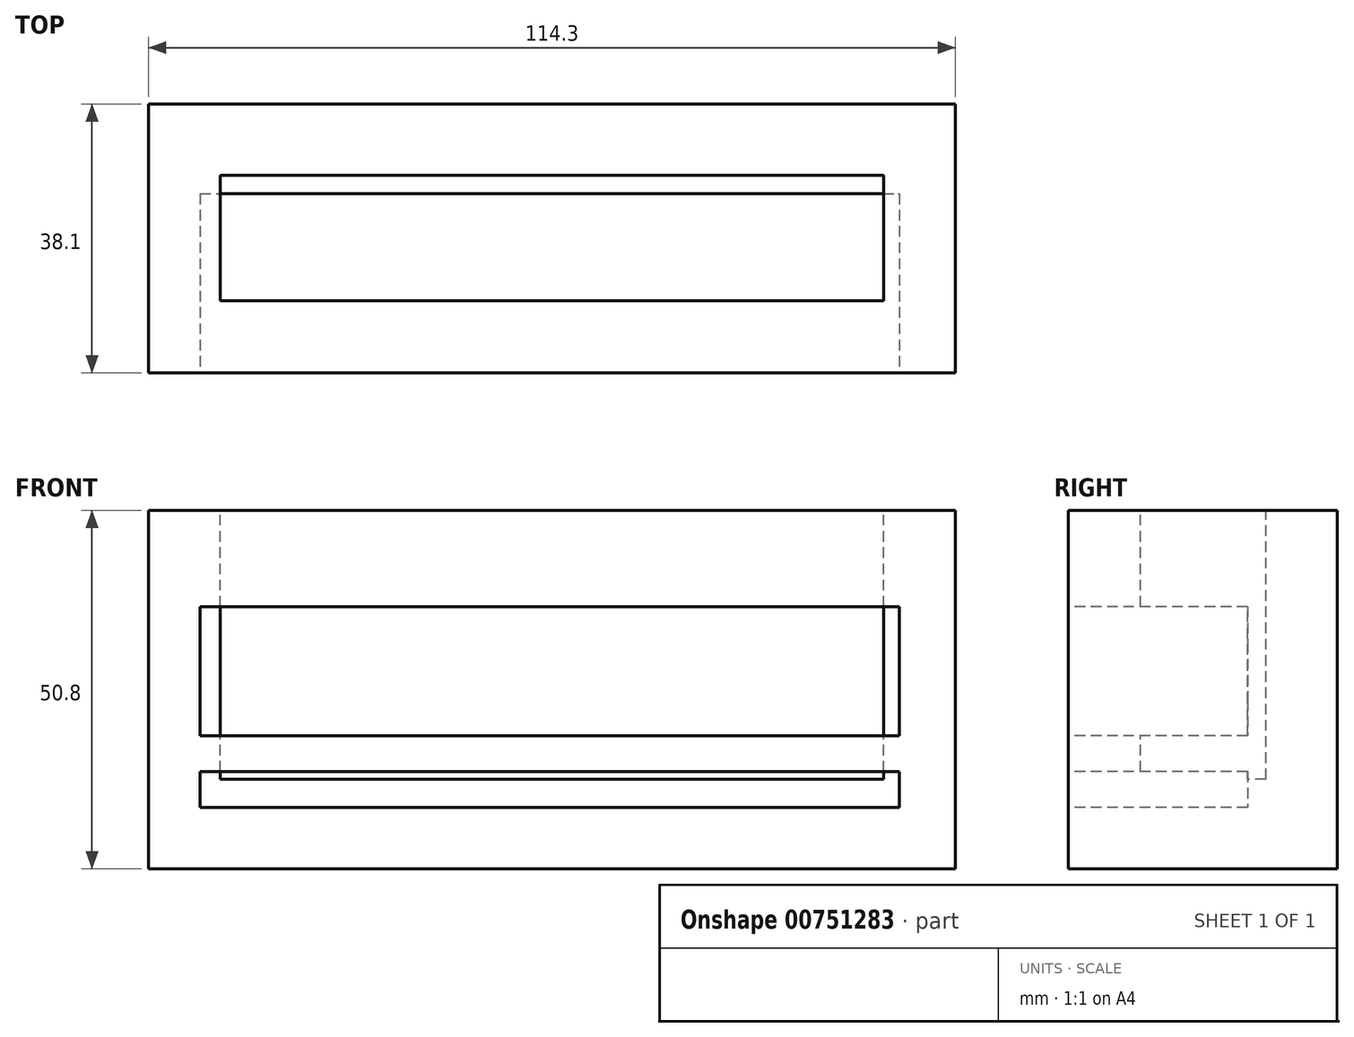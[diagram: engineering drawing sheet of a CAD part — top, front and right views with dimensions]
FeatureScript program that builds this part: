
annotation { "Feature Type Name" : "Feature", "Feature Type Description" : "" }
export const myFeature = defineFeature(function(context is Context, id is Id, definition is map)
    precondition{}
    {
        {
            var Q0;
            Q0=qCreatedBy(makeId("Top.planeOp"),FACE);
            var sketch = newSketch(context, id + "F0", { "sketchPlane" : qUnion([Q0])});
            skLineSegment(sketch, "E0.bottom", {"start": v(-58.02, -10.03) * mm, "end": v(56.28, -10.03) * mm});
            skLineSegment(sketch, "E0.top", {"start": v(-58.02, -48.13) * mm, "end": v(56.28, -48.13) * mm});
            skLineSegment(sketch, "E0.left", {"start": v(-58.02, -10.03) * mm, "end": v(-58.02, -48.13) * mm});
            skLineSegment(sketch, "E0.right", {"start": v(56.28, -10.03) * mm, "end": v(56.28, -48.13) * mm});
            skSolve(sketch);
        }
        {
            var Q0;
            Q0=qSketchRegion(id+"F0",true);
            var Q1;
            Q1 = qSketchRegion(id + "F2", true);
            extrude(context, id + "F1", {"entities" : qUnion([Q0, Q1]), "depth" : 50.8 * mm, "offsetDistance" : 25.4 * mm});
        }
        {
            var Q0;
            Q0=makeQuery(id+"F1.opExtrude","CAP_FACE",FACE,{"disambiguationData":[OSD([sQuery(id+"F0.wireOp",EDGE,"E0.bottom"),sQuery(id+"F0.wireOp",EDGE,"E0.top"),sQuery(id+"F0.wireOp",EDGE,"E0.left"),sQuery(id+"F0.wireOp",EDGE,"E0.right")])],"isStart":false});
            var sketch = newSketch(context, id + "F2", { "sketchPlane" : qUnion([Q0])});
            skLineSegment(sketch, "E1", {"start": v(-58.02, -29.08) * mm, "end": v(56.28, -29.08) * mm, "construction": true});
            skLineSegment(sketch, "E2", {"start": v(-0.87, -10.03) * mm, "end": v(-0.87, -48.13) * mm, "construction": true});
            skLineSegment(sketch, "E3.bottom", {"start": v(-47.88, -20.15) * mm, "end": v(46.1, -20.15) * mm});
            skLineSegment(sketch, "E3.top", {"start": v(-47.88, -37.93) * mm, "end": v(46.1, -37.93) * mm});
            skLineSegment(sketch, "E3.left", {"start": v(-47.88, -20.15) * mm, "end": v(-47.88, -37.93) * mm});
            skLineSegment(sketch, "E3.right", {"start": v(46.1, -20.15) * mm, "end": v(46.1, -37.93) * mm});
            skLineSegment(sketch, "E4", {"start": v(-47.88, -29.04) * mm, "end": v(46.1, -29.04) * mm, "construction": true});
            skLineSegment(sketch, "E5", {"start": v(-0.9, -20.15) * mm, "end": v(-0.9, -37.93) * mm, "construction": true});
            skSolve(sketch);
        }
        {
            var Q0;
            Q0=qSketchRegion(id+"F2",true);
            extrude(context, id + "F3", {"entities" : qUnion([Q0]), "operationType" : NewBodyOperationType.REMOVE, "oppositeDirection" : true, "depth" : 38.1 * mm, "offsetDistance" : 25.4 * mm});
        }
        {
            var Q0;
            Q0=makeQuery(id+"F1.opExtrude","SWEPT_FACE",FACE,{"disambiguationData":[OSD([sQuery(id+"F0.wireOp",EDGE,"E0.top")])]});
            var sketch = newSketch(context, id + "F4", { "sketchPlane" : qUnion([Q0])});
            skLineSegment(sketch, "E6.bottom", {"start": v(-50.75, 13.79) * mm, "end": v(48.3, 13.79) * mm});
            skLineSegment(sketch, "E6.top", {"start": v(-50.75, 8.7) * mm, "end": v(48.3, 8.7) * mm});
            skLineSegment(sketch, "E6.left", {"start": v(-50.75, 13.79) * mm, "end": v(-50.75, 8.7) * mm});
            skLineSegment(sketch, "E6.right", {"start": v(48.3, 13.79) * mm, "end": v(48.3, 8.7) * mm});
            skLineSegment(sketch, "E7", {"start": v(-50.75, 23.95) * mm, "end": v(-50.75, 13.79) * mm, "construction": true});
            skLineSegment(sketch, "E8", {"start": v(48.3, 14.78) * mm, "end": v(48.3, 13.79) * mm, "construction": true});
            skPoint(sketch, "E9.oppositeSnap0", {"position": v(-50.75, 18.87) * mm});
            skLineSegment(sketch, "E9.bottom", {"start": v(-50.75, 23.95) * mm, "end": v(48.3, 23.95) * mm});
            skLineSegment(sketch, "E9.top", {"start": v(-50.75, 18.87) * mm, "end": v(48.3, 18.87) * mm});
            skLineSegment(sketch, "E9.left", {"start": v(-50.75, 23.95) * mm, "end": v(-50.75, 18.87) * mm});
            skLineSegment(sketch, "E9.right", {"start": v(48.3, 23.95) * mm, "end": v(48.3, 18.87) * mm});
            skLineSegment(sketch, "E10.bottom", {"start": v(-50.72, 37.18) * mm, "end": v(48.34, 37.18) * mm});
            skLineSegment(sketch, "E10.top", {"start": v(-50.72, 32.1) * mm, "end": v(48.34, 32.1) * mm});
            skLineSegment(sketch, "E10.left", {"start": v(-50.72, 37.18) * mm, "end": v(-50.72, 32.1) * mm});
            skLineSegment(sketch, "E10.right", {"start": v(48.34, 37.18) * mm, "end": v(48.34, 32.1) * mm});
            skLineSegment(sketch, "E11", {"start": v(-1.22, 23.95) * mm, "end": v(-1.22, 18.87) * mm, "construction": true});
            skLineSegment(sketch, "E12", {"start": v(-1.22, 18.87) * mm, "end": v(-1.22, 13.79) * mm, "construction": true});
            skLineSegment(sketch, "E13", {"start": v(-50.72, 32.1) * mm, "end": v(-50.75, 23.95) * mm, "construction": true});
            skLineSegment(sketch, "E14", {"start": v(48.34, 32.1) * mm, "end": v(48.3, 23.95) * mm, "construction": true});
            skLineSegment(sketch, "E15", {"start": v(48.3, 18.87) * mm, "end": v(48.3, 13.79) * mm, "construction": true});
            skLineSegment(sketch, "E16", {"start": v(-50.75, 18.87) * mm, "end": v(-50.75, 13.79) * mm, "construction": true});
            skLineSegment(sketch, "E17", {"start": v(-50.72, 32.1) * mm, "end": v(-50.75, 23.95) * mm});
            skLineSegment(sketch, "E18", {"start": v(48.34, 32.1) * mm, "end": v(48.3, 23.95) * mm});
            skLineSegment(sketch, "E19", {"start": v(-50.72, 37.18) * mm, "end": v(-56.28, 37.18) * mm});
            skSolve(sketch);
        }
        {
            var Q0;
            Q0=qSketchRegion(id+"F4",true);
            extrude(context, id + "F5", {"entities" : qUnion([Q0]), "operationType" : NewBodyOperationType.REMOVE, "oppositeDirection" : true, "depth" : 25.4 * mm, "offsetDistance" : 25.4 * mm});
        }
        {
            var Q0;
            Q0=qSketchRegion(id+"F4",true);
            extrude(context, id + "F6", {"entities" : qUnion([Q0]), "operationType" : NewBodyOperationType.REMOVE, "oppositeDirection" : true, "depth" : 25.4 * mm, "offsetDistance" : 25.4 * mm});
        }
    });
